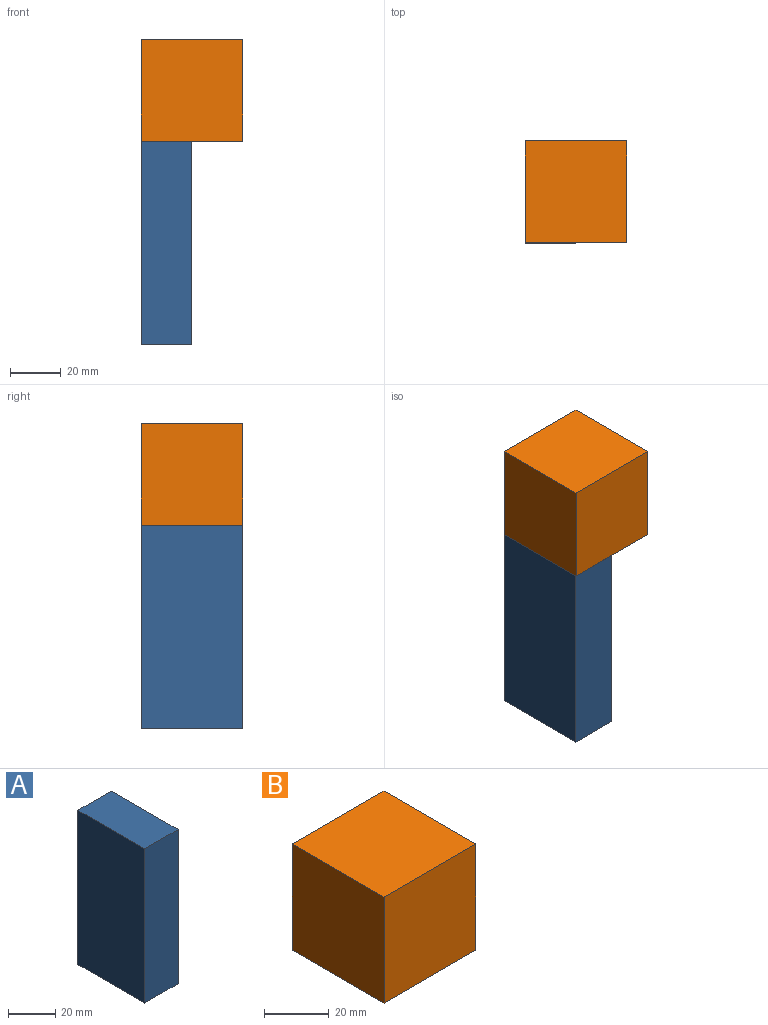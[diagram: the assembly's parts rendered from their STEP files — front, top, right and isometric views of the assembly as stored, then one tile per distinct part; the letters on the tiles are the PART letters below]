
ASSEMBLY  parts=2 mates=1
PART A: 6 faces, bbox 20x40x80 mm
  f0: plane 80x40mm, normal (-1,0,0), area 3200mm2, adj f1,f3,f4,f5
  f1: plane 80x20mm, normal (0,-1,0), area 1600mm2, adj f0,f2,f4,f5
  f2: plane 80x40mm, normal (1,0,0), area 3200mm2, adj f1,f3,f4,f5
  f3: plane 80x20mm, normal (0,1,0), area 1600mm2, adj f0,f2,f4,f5
  f4: plane 40x20mm, normal (0,0,1), area 800mm2, adj f0,f1,f2,f3
  f5: plane 40x20mm, normal (0,0,-1), area 800mm2, adj f0,f1,f2,f3
PART B: 6 faces, bbox 40x40x40 mm
  f0: plane 40x40mm, normal (-1,0,0), area 1600mm2, adj f1,f3,f4,f5
  f1: plane 40x40mm, normal (0,-1,0), area 1600mm2, adj f0,f2,f4,f5
  f2: plane 40x40mm, normal (1,0,0), area 1600mm2, adj f1,f3,f4,f5
  f3: plane 40x40mm, normal (0,1,0), area 1600mm2, adj f0,f2,f4,f5
  f4: plane 40x40mm, normal (0,0,1), area 1600mm2, adj f0,f1,f2,f3
  f5: plane 40x40mm, normal (0,0,-1), area 1600mm2, adj f0,f1,f2,f3
PLACE A t=(49.68,52.78,15.62)mm
PLACE B rot(axis=(1,0,0),180deg) t=(-17.96,30.05,135.62)mm
MATE fastened B.f4 <-> A.f4  axis (0,0,-1) through (-17.96,10.05,95.62)mm
